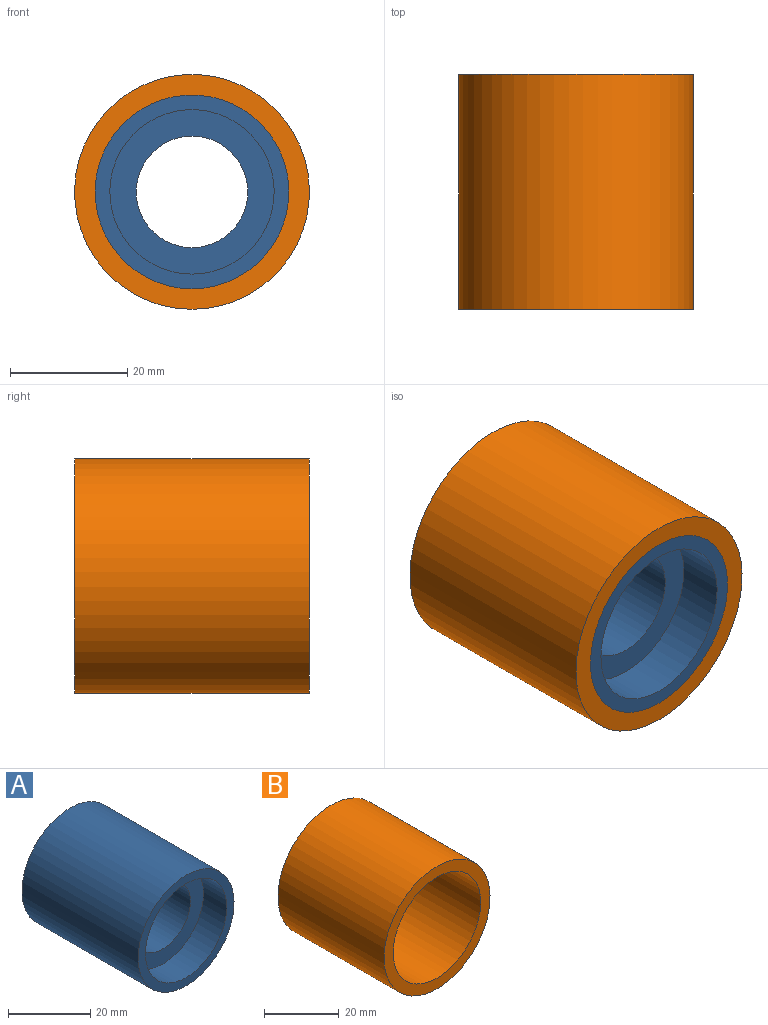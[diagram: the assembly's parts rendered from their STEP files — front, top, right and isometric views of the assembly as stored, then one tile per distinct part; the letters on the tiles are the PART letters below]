
ASSEMBLY  parts=2 mates=1
PART A: 8 faces, bbox 33x40x33 mm
  f0: cylinder r=9.5mm len=24mm, axis (0,1,0), area 1432.6mm2, adj f5,f7
  f1: cylinder r=16.5mm len=40mm, axis (0,1,0), area 4146.9mm2, adj f2,f3
  f2: plane 33x33mm, normal (0,-1,0), area 239.5mm2, adj f1,f4
  f3: plane 33x33mm, normal (0,1,0), area 239.5mm2, adj f1,f6
  f4: cylinder r=14mm len=28mm, axis (0,-1,0), area 703.7mm2, adj f2,f5
  f5: plane 28x28mm, normal (0,-1,0), area 332.2mm2, adj f0,f4
  f6: cylinder r=14mm len=28mm, axis (0,1,0), area 703.7mm2, adj f3,f7
  f7: plane 28x28mm, normal (0,1,0), area 332.2mm2, adj f0,f6
PART B: 4 faces, bbox 40x40x40 mm
  f0: cylinder r=16.5mm len=40mm, axis (0,1,0), area 4146.9mm2, adj f2,f3
  f1: cylinder r=20mm len=40mm, axis (0,1,0), area 5026.5mm2, adj f2,f3
  f2: plane 40x40mm, normal (0,-1,0), area 401.3mm2, adj f0,f1
  f3: plane 40x40mm, normal (0,1,0), area 401.3mm2, adj f0,f1
PLACE A t=(0.28,19.88,-0.42)mm fixed
PLACE B t=(0.28,19.88,-0.42)mm
MATE fastened A.f1 <-> B.f0  axis (0,1,0) through (0.28,-0.12,-0.42)mm
